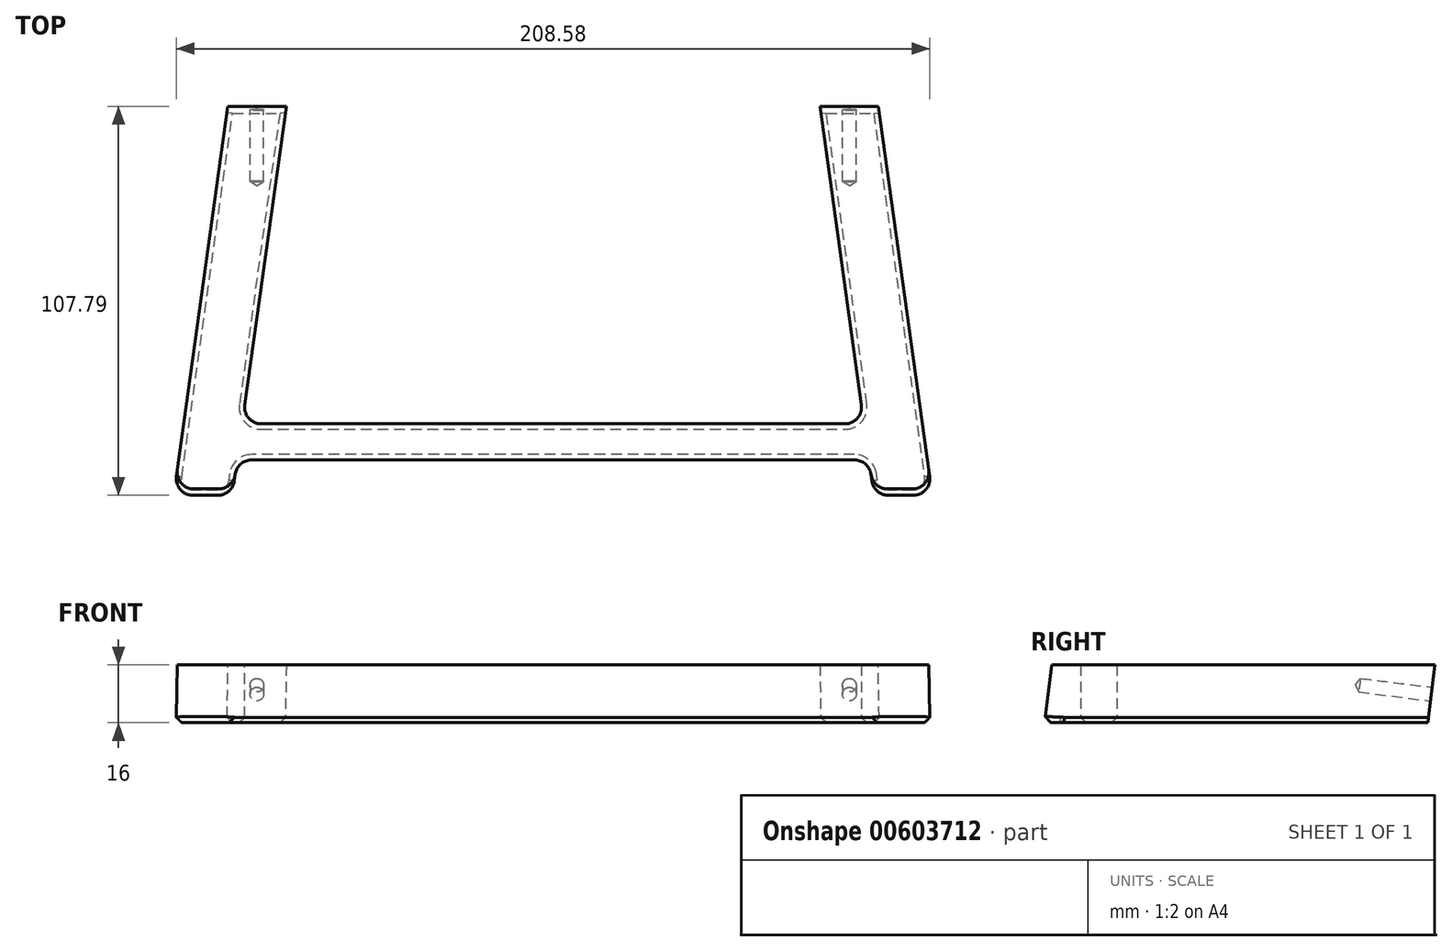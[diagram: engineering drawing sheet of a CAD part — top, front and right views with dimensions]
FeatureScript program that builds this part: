
annotation { "Feature Type Name" : "Feature", "Feature Type Description" : "" }
export const myFeature = defineFeature(function(context is Context, id is Id, definition is map)
    precondition{}
    {
        {
            var Q0;
            Q0=qCreatedBy(makeId("Top.planeOp"),FACE);
            var sketch = newSketch(context, id + "F0", { "sketchPlane" : qUnion([Q0])});
            skLineSegment(sketch, "E0", {"start": v(0, 0) * mm, "end": v(0, 135) * mm, "construction": true});
            skLineSegment(sketch, "E1", {"start": v(-105, 0) * mm, "end": v(-90, 108) * mm});
            skLineSegment(sketch, "E2", {"start": v(-90, 108) * mm, "end": v(-73.85, 108) * mm});
            skLineSegment(sketch, "E3", {"start": v(-73.85, 108) * mm, "end": v(-86.07, 20) * mm});
            skLineSegment(sketch, "E4", {"start": v(0, 10) * mm, "end": v(-87.46, 10) * mm});
            skLineSegment(sketch, "E5", {"start": v(0, 20) * mm, "end": v(-86.07, 20) * mm});
            skLineSegment(sketch, "E6", {"start": v(-105, 0) * mm, "end": v(-88.85, 0) * mm});
            skLineSegment(sketch, "E7.trimOffspring", {"start": v(-87.46, 10) * mm, "end": v(-88.85, 0) * mm});
            skLineSegment(sketch, "E8.MirrorCS", {"start": v(90, 108) * mm, "end": v(73.85, 108) * mm});
            skLineSegment(sketch, "E9.MirrorCS", {"start": v(105, 0) * mm, "end": v(90, 108) * mm});
            skLineSegment(sketch, "E10.MirrorCS", {"start": v(87.46, 10) * mm, "end": v(88.85, 0) * mm});
            skLineSegment(sketch, "E11.MirrorCS", {"start": v(0, 10) * mm, "end": v(87.46, 10) * mm});
            skLineSegment(sketch, "E12.MirrorCS", {"start": v(0, 20) * mm, "end": v(86.07, 20) * mm});
            skLineSegment(sketch, "E13.MirrorCS", {"start": v(73.85, 108) * mm, "end": v(86.07, 20) * mm});
            skLineSegment(sketch, "E14.MirrorCS", {"start": v(105, 0) * mm, "end": v(88.85, 0) * mm});
            skSolve(sketch);
        }
        {
            var Q0;
            Q0 = qSketchRegion(id + "F0", true);
            extrude(context, id + "F1", {"entities" : qUnion([Q0]), "endBound" : BoundingType.SYMMETRIC, "depth" : 16 * mm, "offsetDistance" : 25 * mm});
        }
        {
            var Q0;
            Q0=qCreatedBy(makeId("Right.planeOp"),FACE);
            var sketch = newSketch(context, id + "F2", { "sketchPlane" : qUnion([Q0])});
            skLineSegment(sketch, "E15", {"start": v(0, 0) * mm, "end": v(88.44, 0) * mm, "construction": true});
            skLineSegment(sketch, "E16", {"start": v(0, 0) * mm, "end": v(0, 8) * mm});
            skLineSegment(sketch, "E17", {"start": v(0, 8) * mm, "end": v(1.96, 8) * mm});
            skLineSegment(sketch, "E18", {"start": v(1.96, 8) * mm, "end": v(0, -8) * mm});
            skLineSegment(sketch, "E19", {"start": v(0, -8) * mm, "end": v(0, 0) * mm});
            skLineSegment(sketch, "E20", {"start": v(108, 0) * mm, "end": v(108, -8) * mm});
            skLineSegment(sketch, "E21", {"start": v(108, -8) * mm, "end": v(106.04, -8) * mm});
            skLineSegment(sketch, "E22", {"start": v(108, 0) * mm, "end": v(108, 8) * mm});
            skLineSegment(sketch, "E23", {"start": v(108, 8) * mm, "end": v(106.04, -8) * mm});
            skSolve(sketch);
        }
        {
            var Q0;
            Q0 = qSketchRegion(id + "F2", true);
            extrude(context, id + "F3", {"entities" : qUnion([Q0]), "operationType" : NewBodyOperationType.REMOVE, "endBound" : BoundingType.SYMMETRIC, "oppositeDirection" : true, "depth" : 500 * mm, "offsetDistance" : 25 * mm});
        }
        {
            var Q0;
            {var subQ5=sQuery(id+"F0.wireOp",EDGE,"E9.MirrorCS");Q0=makeQuery(id+"F3.boolean.opBoolean","COPY",FACE,{"disambiguationData":[TD([makeQuery(id+"F1.opExtrude","SWEPT_FACE",FACE,{"disambiguationData":[OSD([subQ5])]})])],"derivedFrom":makeQuery(id+"F3.opExtrude","SWEPT_FACE",FACE,{"disambiguationData":[OSD([sQuery(id+"F2.wireOp",EDGE,"E23")])]})});}
            var sketch = newSketch(context, id + "F4", { "sketchPlane" : qUnion([Q0])});
            skPoint(sketch, "E24", {"position": v(-82, 12.98) * mm});
            skPoint(sketch, "E25", {"position": v(82, 12.98) * mm});
            skSolve(sketch);
        }
        {
            var Q0;
            Q0=sQuery(id+"F4.wireOp",VERTEX,"E24");
            var Q1;
            Q1=sQuery(id+"F4.wireOp",VERTEX,"E25");
            var Q2;
            Q2=makeQuery(id+"F1.opExtrude","SWEPT_BODY",BODY,{"disambiguationData":[OSD([sQuery(id+"F0.wireOp",EDGE,"E1"),sQuery(id+"F0.wireOp",EDGE,"E2"),sQuery(id+"F0.wireOp",EDGE,"E3"),sQuery(id+"F0.wireOp",EDGE,"E4"),sQuery(id+"F0.wireOp",EDGE,"E5"),sQuery(id+"F0.wireOp",EDGE,"E6"),sQuery(id+"F0.wireOp",EDGE,"E7.trimOffspring"),sQuery(id+"F0.wireOp",EDGE,"E8.MirrorCS"),sQuery(id+"F0.wireOp",EDGE,"E9.MirrorCS"),sQuery(id+"F0.wireOp",EDGE,"E10.MirrorCS"),sQuery(id+"F0.wireOp",EDGE,"E11.MirrorCS"),sQuery(id+"F0.wireOp",EDGE,"E12.MirrorCS"),sQuery(id+"F0.wireOp",EDGE,"E13.MirrorCS"),sQuery(id+"F0.wireOp",EDGE,"E14.MirrorCS")])]});
            hole(context, id + "F5", {"style" : HoleStyle.SIMPLE, "endStyle" : HoleEndStyle.BLIND, "holeDiameter" : 3.8 * mm, "majorDiameter" : 5 * mm, "holeDepth" : 20 * mm, "isTappedThrough" : true, "tappedDepth" : 12 * mm, "tapClearance" : 3, "startFromSketch" : true, "locations" : qUnion([Q0, Q1]), "scope" : qUnion([Q2])});
        }
        {
            var Q0;
            Q0=makeQuery(id+"F1.opExtrude","SWEPT_EDGE",EDGE,{"disambiguationData":[OSD([sQuery(id+"F0.wireOp",EDGE,"E12.MirrorCS"),sQuery(id+"F0.wireOp",EDGE,"E13.MirrorCS")])]});
            var Q1;
            Q1=makeQuery(id+"F1.opExtrude","SWEPT_EDGE",EDGE,{"disambiguationData":[OSD([sQuery(id+"F0.wireOp",EDGE,"E10.MirrorCS"),sQuery(id+"F0.wireOp",EDGE,"E11.MirrorCS")])]});
            var Q2;
            Q2=makeQuery(id+"F3.boolean.opBoolean","INTERSECT",EDGE,{"derivedFrom":[makeQuery(id+"F1.opExtrude","SWEPT_FACE",FACE,{"disambiguationData":[OSD([sQuery(id+"F0.wireOp",EDGE,"E9.MirrorCS")])]}),makeQuery(id+"F3.opExtrude","SWEPT_FACE",FACE,{"disambiguationData":[OSD([sQuery(id+"F2.wireOp",EDGE,"E18")])]})]});
            var Q3;
            Q3=makeQuery(id+"F3.boolean.opBoolean","INTERSECT",EDGE,{"derivedFrom":[makeQuery(id+"F1.opExtrude","SWEPT_FACE",FACE,{"disambiguationData":[OSD([sQuery(id+"F0.wireOp",EDGE,"E10.MirrorCS")])]}),makeQuery(id+"F3.opExtrude","SWEPT_FACE",FACE,{"disambiguationData":[OSD([sQuery(id+"F2.wireOp",EDGE,"E18")])]})]});
            var Q4;
            Q4=makeQuery(id+"F1.opExtrude","SWEPT_EDGE",EDGE,{"disambiguationData":[OSD([sQuery(id+"F0.wireOp",EDGE,"E4"),sQuery(id+"F0.wireOp",EDGE,"E7.trimOffspring")])]});
            var Q5;
            Q5=makeQuery(id+"F3.boolean.opBoolean","INTERSECT",EDGE,{"derivedFrom":[makeQuery(id+"F1.opExtrude","SWEPT_FACE",FACE,{"disambiguationData":[OSD([sQuery(id+"F0.wireOp",EDGE,"E7.trimOffspring")])]}),makeQuery(id+"F3.opExtrude","SWEPT_FACE",FACE,{"disambiguationData":[OSD([sQuery(id+"F2.wireOp",EDGE,"E18")])]})]});
            var Q6;
            Q6=makeQuery(id+"F3.boolean.opBoolean","INTERSECT",EDGE,{"derivedFrom":[makeQuery(id+"F1.opExtrude","SWEPT_FACE",FACE,{"disambiguationData":[OSD([sQuery(id+"F0.wireOp",EDGE,"E1")])]}),makeQuery(id+"F3.opExtrude","SWEPT_FACE",FACE,{"disambiguationData":[OSD([sQuery(id+"F2.wireOp",EDGE,"E18")])]})]});
            var Q7;
            Q7=makeQuery(id+"F1.opExtrude","SWEPT_EDGE",EDGE,{"disambiguationData":[OSD([sQuery(id+"F0.wireOp",EDGE,"E3"),sQuery(id+"F0.wireOp",EDGE,"E5")])]});
            fillet(context, id + "F6", {"entities" : qUnion([Q0, Q1, Q2, Q3, Q4, Q5, Q6, Q7]), "tangentPropagation" : true, "radius" : 4.6 * mm, "defaultsChanged" : true, "vertexSettings" : [], "allowEdgeOverflow" : false});
        }
        {
            var Q0;
            Q0=makeQuery(id+"F1.opExtrude","CAP_EDGE",EDGE,{"disambiguationData":[OSD([sQuery(id+"F0.wireOp",EDGE,"E5"),sQuery(id+"F0.wireOp",EDGE,"E12.MirrorCS")])],"isStart":true});
            var Q1;
            Q1=makeQuery(id+"F1.opExtrude","CAP_EDGE",EDGE,{"disambiguationData":[OSD([sQuery(id+"F0.wireOp",EDGE,"E4"),sQuery(id+"F0.wireOp",EDGE,"E11.MirrorCS")])],"isStart":true});
            chamfer(context, id + "F7", {"entities" : qUnion([Q0, Q1]), "width" : 1.5 * mm, "tangentPropagation" : true});
        }
    });
